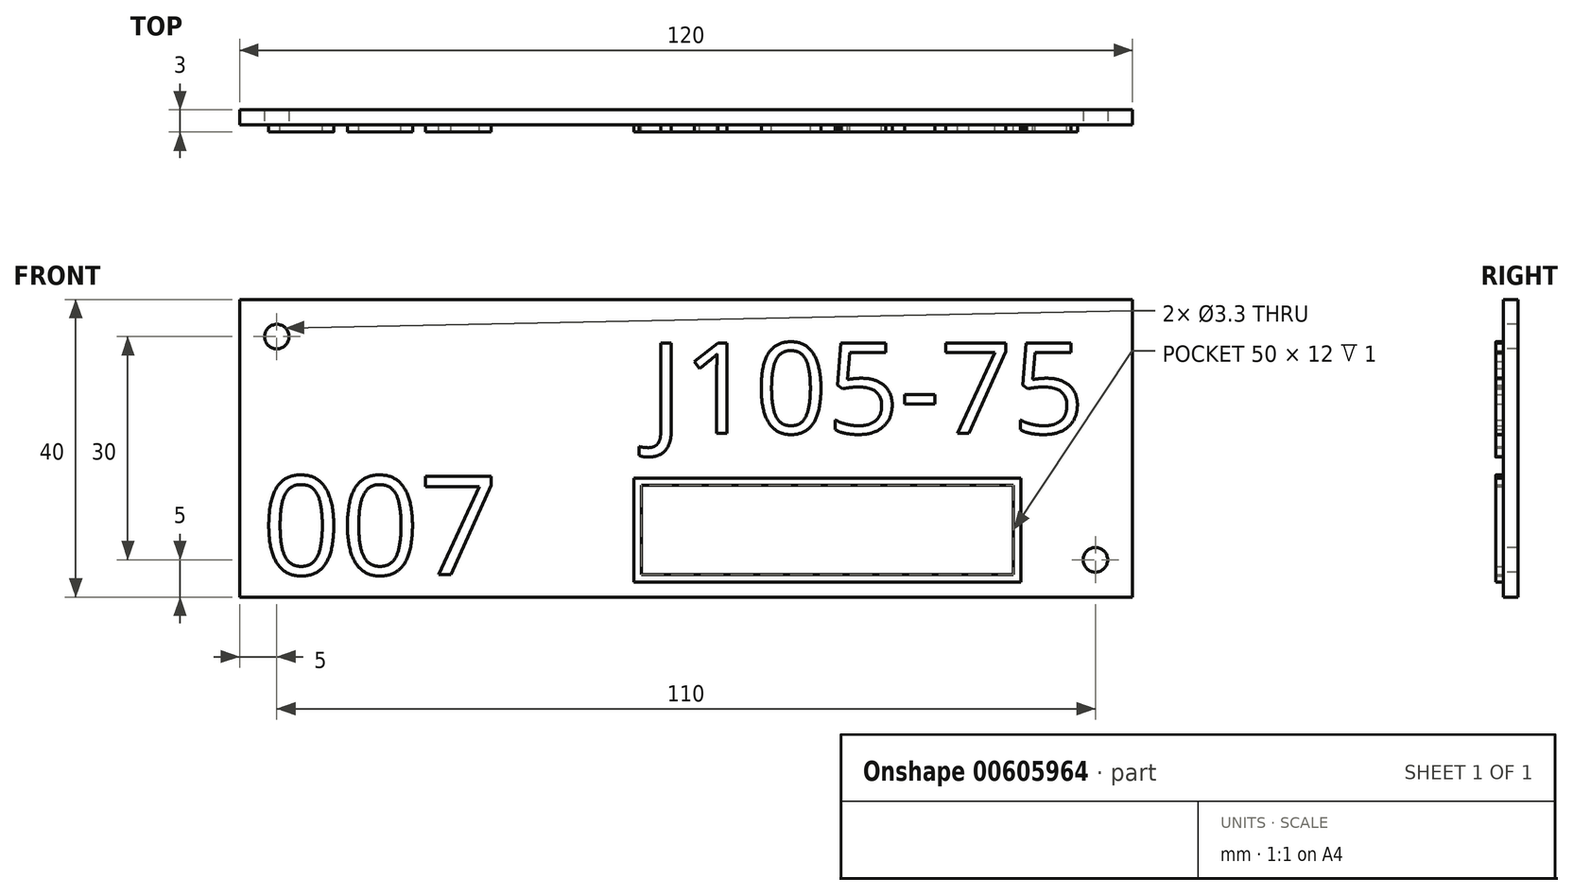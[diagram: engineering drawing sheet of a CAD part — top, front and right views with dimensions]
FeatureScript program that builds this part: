
annotation { "Feature Type Name" : "Feature", "Feature Type Description" : "" }
export const myFeature = defineFeature(function(context is Context, id is Id, definition is map)
    precondition{}
    {
        {
            var Q0;
            Q0=qCreatedBy(makeId("Front.planeOp"),FACE);
            var sketch = newSketch(context, id + "F0", { "sketchPlane" : qUnion([Q0])});
            skLineSegment(sketch, "E0.bottom", {"start": v(60, -20) * mm, "end": v(-60, -20) * mm});
            skLineSegment(sketch, "E0.top", {"start": v(60, 20) * mm, "end": v(-60, 20) * mm});
            skLineSegment(sketch, "E0.left", {"start": v(60, -20) * mm, "end": v(60, 20) * mm});
            skLineSegment(sketch, "E0.right", {"start": v(-60, -20) * mm, "end": v(-60, 20) * mm});
            skPoint(sketch, "E0.middle", {"position": v(0, 0) * mm});
            skSolve(sketch);
        }
        {
            var Q0;
            Q0=makeQuery(id+"F0.imprint","IMPRINT",FACE,{"disambiguationData":[TD([[makeQuery(id+"F0.imprint","IMPRINT",EDGE,{"derivedFrom":sQuery(id+"F0.wireOp",EDGE,"E0.bottom")}),-1.0]])]});
            extrude(context, id + "F1", {"entities" : qUnion([Q0]), "depth" : 2 * mm});
        }
        {
            var Q0;
            Q0=makeQuery(id+"F1.opExtrude","CAP_FACE",FACE,{"disambiguationData":[OSD([sQuery(id+"F0.wireOp",EDGE,"E0.bottom"),sQuery(id+"F0.wireOp",EDGE,"E0.top"),sQuery(id+"F0.wireOp",EDGE,"E0.left"),sQuery(id+"F0.wireOp",EDGE,"E0.right")])],"isStart":false});
            var sketch = newSketch(context, id + "F2", { "sketchPlane" : qUnion([Q0])});
            skPoint(sketch, "E1", {"position": v(-55, 15) * mm});
            skPoint(sketch, "E2", {"position": v(55, -15) * mm});
            skSolve(sketch);
        }
        {
            var Q0;
            Q0=sQuery(id+"F2.wireOp",VERTEX,"E1");
            var Q1;
            Q1=sQuery(id+"F2.wireOp",VERTEX,"E2");
            var Q2;
            Q2=makeQuery(id+"F1.opExtrude","SWEPT_BODY",BODY,{"disambiguationData":[OSD([sQuery(id+"F0.wireOp",EDGE,"E0.bottom"),sQuery(id+"F0.wireOp",EDGE,"E0.top"),sQuery(id+"F0.wireOp",EDGE,"E0.left"),sQuery(id+"F0.wireOp",EDGE,"E0.right")])]});
            hole(context, id + "F3", {"style" : HoleStyle.SIMPLE, "endStyle" : HoleEndStyle.THROUGH, "holeDiameter" : 3.3 * mm, "locations" : qUnion([Q0, Q1]), "scope" : qUnion([Q2]), "isTappedThrough" : true});
        }
        {
            var Q0;
            Q0=makeQuery(id+"F1.opExtrude","CAP_FACE",FACE,{"disambiguationData":[OSD([sQuery(id+"F0.wireOp",EDGE,"E0.bottom"),sQuery(id+"F0.wireOp",EDGE,"E0.top"),sQuery(id+"F0.wireOp",EDGE,"E0.left"),sQuery(id+"F0.wireOp",EDGE,"E0.right")])],"isStart":false});
            var sketch = newSketch(context, id + "F4", { "sketchPlane" : qUnion([Q0])});
            skText(sketch, "E3", { "text": "J105-75", "fontName": "OpenSans-Regular.ttf"});
            const initialGuessF4  = {"E3": [-0.005, 0.002, 1, 0, 0.01223]};
            skSetInitialGuess(sketch, initialGuessF4);
            skSolve(sketch);
        }
        {
            var Q0;
            Q0=qSketchRegion(id+"F4",true);
            extrude(context, id + "F5", {"entities" : qUnion([Q0]), "operationType" : NewBodyOperationType.ADD, "depth" : 1 * mm});
        }
        {
            var Q0;
            {var subQ0=sQuery(id+"F0.wireOp",EDGE,"E0.top");var subQ1=sQuery(id+"F0.wireOp",EDGE,"E0.left");var subQ2=sQuery(id+"F0.wireOp",EDGE,"E0.right");var subQ3=sQuery(id+"F0.wireOp",EDGE,"E0.bottom");Q0=makeQuery(id+"F5.boolean.opBoolean","SPLIT",FACE,{"disambiguationData":[TD([makeQuery(id+"F1.opExtrude","SWEPT_FACE",FACE,{"disambiguationData":[OSD([subQ3])]})])],"derivedFrom":makeQuery(id+"F1.opExtrude","CAP_FACE",FACE,{"disambiguationData":[OSD([subQ3,subQ0,subQ1,subQ2])],"isStart":false})});}
            var sketch = newSketch(context, id + "F6", { "sketchPlane" : qUnion([Q0])});
            skText(sketch, "E4", { "text": "007", "fontName": "OpenSans-Regular.ttf"});
            const initialGuessF6  = {"E4": [-0.057, -0.017, 1, 0, 0.01332]};
            skSetInitialGuess(sketch, initialGuessF6);
            skSolve(sketch);
        }
        {
            var Q0;
            Q0=qSketchRegion(id+"F6",true);
            extrude(context, id + "F7", {"entities" : qUnion([Q0]), "operationType" : NewBodyOperationType.ADD, "depth" : 1 * mm});
        }
        {
            var Q0;
            {var subQ46=sQuery(id+"F0.wireOp",EDGE,"E0.top");var subQ48=sQuery(id+"F0.wireOp",EDGE,"E0.left");var subQ66=sQuery(id+"F0.wireOp",EDGE,"E0.right");var subQ76=sQuery(id+"F0.wireOp",EDGE,"E0.bottom");var subQ77=makeQuery(id+"F1.opExtrude","SWEPT_FACE",FACE,{"disambiguationData":[OSD([subQ76])]});Q0=makeQuery(id+"F7.boolean.opBoolean","SPLIT",FACE,{"disambiguationData":[TD([subQ77])],"derivedFrom":makeQuery(id+"F5.boolean.opBoolean","SPLIT",FACE,{"disambiguationData":[TD([subQ77])],"derivedFrom":makeQuery(id+"F1.opExtrude","CAP_FACE",FACE,{"disambiguationData":[OSD([subQ76,subQ46,subQ48,subQ66])],"isStart":false})})});}
            var sketch = newSketch(context, id + "F8", { "sketchPlane" : qUnion([Q0])});
            skLineSegment(sketch, "E5.bottom", {"start": v(45, -18) * mm, "end": v(-7, -18) * mm});
            skLineSegment(sketch, "E5.top", {"start": v(45, -4) * mm, "end": v(-7, -4) * mm});
            skLineSegment(sketch, "E5.left", {"start": v(45, -18) * mm, "end": v(45, -4) * mm});
            skLineSegment(sketch, "E5.right", {"start": v(-7, -18) * mm, "end": v(-7, -4) * mm});
            skPoint(sketch, "E5.middle", {"position": v(19, -11) * mm});
            skLineSegment(sketch, "E6.0", {"start": v(44, -5) * mm, "end": v(-6, -5) * mm});
            skLineSegment(sketch, "E6.1", {"start": v(44, -17) * mm, "end": v(44, -5) * mm});
            skLineSegment(sketch, "E6.2", {"start": v(44, -17) * mm, "end": v(-6, -17) * mm});
            skLineSegment(sketch, "E6.3", {"start": v(-6, -17) * mm, "end": v(-6, -5) * mm});
            skSolve(sketch);
        }
        {
            var Q0;
            Q0=makeQuery(id+"F8.imprint","IMPRINT",FACE,{"disambiguationData":[TD([[makeQuery(id+"F8.imprint","IMPRINT",EDGE,{"derivedFrom":sQuery(id+"F8.wireOp",EDGE,"E5.bottom")}),-1.0]])]});
            extrude(context, id + "F9", {"entities" : qUnion([Q0]), "operationType" : NewBodyOperationType.ADD, "depth" : 1 * mm});
        }
    });
